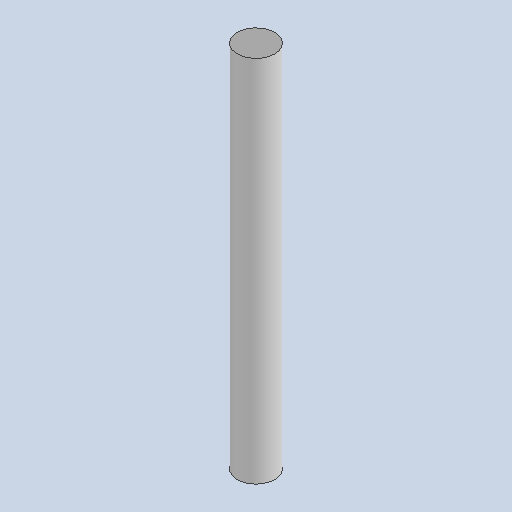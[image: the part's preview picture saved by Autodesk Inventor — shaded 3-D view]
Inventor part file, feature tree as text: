
AUTODESK INVENTOR PART (.ipt)
format: ipt  version: 2025 (Build 290162010, 162A)  size: 77,824 bytes
history: native  units: mm
features: extrude x1, sketch x1
ambient origin geometry x8: Origin, YZ Plane, XZ Plane, XY Plane, X Axis, Y Axis, Z Axis, Center Point
bodies: Solid1 (feature_tree)
feature tree (2):
  extrude  "Extrusion1"  Depth=118.0mm TaperAngle=0.0deg
  sketch  "Sketch1"  dims[d0=12.0mm d1=118.0mm d2=40.0mm d3=0.0mm d4=0.0mm]
